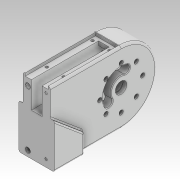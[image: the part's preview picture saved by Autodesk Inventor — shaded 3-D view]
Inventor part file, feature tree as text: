
AUTODESK INVENTOR PART (.ipt)
format: ipt  version: 2020 (Build 240168000, 168)  size: 836,608 bytes
history: native  units: mm
features: sketch x30, extrude x28, fillet x5, plane x2, revolve x2, pattern_circular x1, chamfer x1, projected_geometry x1
ambient origin geometry x8: Origin, YZ Plane, XZ Plane, XY Plane, X Axis, Y Axis, Z Axis, Center Point
bodies: Solid1 (feature_tree)
feature tree (70):
  extrude  "Extrusion1"  Depth=250.0mm
  extrude  "Extrusion3"  Depth=50.0mm TaperAngle=0.0deg
  extrude  "Extrusion6"  TaperAngle=0.0deg  [1 undecoded]
  extrude  "Extrusion7"  Depth=50.0mm
  extrude  "Extrusion8"  Depth=10.0mm TaperAngle=0.0deg
  extrude  "Extrusion9"  TaperAngle=0.0deg  [1 undecoded]
  extrude  "Extrusion10"  TaperAngle=30.0deg  [1 undecoded]
  extrude  "Extrusion11"  Depth=16.15mm
  extrude  "Extrusion12"  Depth=60.0mm
  plane  "Work Plane1"
  extrude  "Extrusion13"  Depth=10.0mm TaperAngle=0.0deg
  revolve  "Revolution1"  [1 undecoded]
  extrude  "Extrusion14"  Depth=86.0mm
  extrude  "Extrusion15"  Depth=4.0mm TaperAngle=0.0deg
  extrude  "Extrusion16"  Depth=70.0mm
  revolve  "Revolution2"  [1 undecoded]
  extrude  "Extrusion17"  Depth=7.3mm
  fillet  "Fillet1"  [1 undecoded]
  plane  "Work Plane2"
  extrude  "Extrusion18"  Depth=34.0mm
  extrude  "Extrusion19"  Depth=3.0mm TaperAngle=0.0deg
  extrude  "Extrusion20"  Depth=15.0mm TaperAngle=0.0deg
  extrude  "Extrusion21"  Depth=15.0mm
  extrude  "Extrusion25"  Depth=80.0mm TaperAngle=360.0deg
  extrude  "Extrusion22"  Depth=5.2mm
  fillet  "Fillet2"  Radius=5.2mm
  fillet  "Fillet3"  Radius=1.0mm
  extrude  "Extrusion23"  TaperAngle=90.0deg  [1 undecoded]
  extrude  "Extrusion24"  Depth=5.5mm
  extrude  "Extrusion26"  Depth=19.198622mm
  extrude  "Extrusion27"  Depth=50.0mm
  extrude  "Extrusion28"  TaperAngle=0.0deg  [1 undecoded]
  extrude  "CHOP"  Depth=14.0mm
  extrude  "Extrusion30"  Depth=12.5mm
  extrude  "Extrusion31"  Depth=1.0mm
  fillet  "Fillet4"  Radius=10.0mm
  pattern_circular  "Circular Pattern1"  [2 undecoded]
  chamfer  "Chamfer1"  Distance=32.0mm
  fillet  "Fillet5"  Radius=110.0mm
  sketch  "Sketch1"  dims[d0=50.0mm d1=250.0mm]
  sketch  "Sketch3"  dims[d2=47.2mm d3=50.0mm d4=0.0mm]
  sketch  "Sketch6"  dims[d10=5.0mm d11=0.0mm d12=0.0mm]
  sketch  "Sketch7"  dims[d19=50.0mm d20=0.0mm d21=8.726646mm]
  projected_geometry  "Projected Loop1"
  sketch  "Sketch8"  dims[d22=75.0mm d25=10.0mm d26=0.0mm]
  sketch  "Sketch9"  dims[d27=50.0mm d30=0.0mm d31=0.0mm]
  sketch  "Sketch10"  dims[d33=30.0deg d34=30.0deg]
  sketch  "Sketch11"  dims[d35=0.0mm d36=0.0mm d37=16.15mm]
  sketch  "Sketch12"  dims[d38=3.3mm d39=60.0mm]
  sketch  "Sketch13"  dims[d40=80.0mm d42=360.0deg d44=10.0mm d45=0.0mm]
  sketch  "Sketch14"  dims[d50=42.0mm d51=42.0mm d52=0.0mm d53=0.0mm]
  sketch  "Sketch15"  dims[d54=38.0mm d55=86.0mm]
  sketch  "Sketch16"  dims[d56=59.0mm d57=4.0mm d58=0.0mm]
  sketch  "Sketch17"  dims[d59=-2.0mm d60=70.0mm]
  sketch  "Sketch18"  dims[d61=40.0mm d62=18.0mm d63=0.0mm]
  sketch  "Sketch19"  dims[d64=1.5mm d65=7.3mm d66=90.0deg]
  sketch  "Sketch20"  dims[d67=22.0mm d68=34.0mm]
  sketch  "Sketch21"  dims[d69=3.5mm d70=3.0mm d71=0.0mm]
  sketch  "Sketch22"  dims[d72=0.0mm d73=15.0mm d74=0.0mm]
  sketch  "Sketch23"  dims[d75=15.0mm d76=130.0mm]
  sketch  "Sketch24"  dims[d77=6.0mm d78=80.0mm d80=360.0deg]
  sketch  "Sketch25"  dims[d82=15.0mm d83=0.0mm d84=5.2mm d85=5.2mm d86=1.0mm]
  sketch  "Sketch26"  dims[d87=1.5mm d88=90.0deg]
  sketch  "Sketch27"  dims[d89=5.5mm d90=20.0mm]
  sketch  "Sketch28"  dims[d91=30.0deg d92=19.198622mm]
  sketch  "Sketch29"  dims[d93=15.0mm d94=0.0mm d95=50.0mm]
  sketch  "Sketch30"  dims[d96=30.0mm d97=0.0mm]
  sketch  "Sketch31"  dims[d98=8.0mm d99=14.0mm]
  sketch  "Sketch32"  dims[d100=6.4mm d101=12.5mm]
  sketch  "Sketch33"  dims[d102=130.0mm d103=80.0mm d104=0.0mm d105=0.0mm d106=2.45mm d107=10.0mm d108=10.0mm d109=32.0mm d110=110.0mm d111=0.0mm d112=3.0mm d113=3.0mm d114=5.0mm d115=1.0mm d116=4.0mm d117=0.0mm d118=4.0mm d119=4.0mm d120=32.25mm d121=0.0mm d122=3.0mm d124=0.5mm d125=0.0mm d126=3.0mm d127=2.0mm d128=8.0mm d129=8.0mm d130=4.0mm d131=4.0mm d132=3.9mm d133=6.0mm d134=0.0mm d135=4.0mm d136=0.0mm d137=60.0mm d138=0.5mm d139=0.0mm d140=3.0mm d141=10.0mm d142=20.0mm d143=15.0mm d144=0.0mm d145=8.0mm d146=23.75mm d147=0.0mm d148=15.0mm d149=23.75mm d150=0.0mm d151=200.998mm d152=0.0mm d153=76.0mm d154=4.0mm d155=1.0mm d156=0.0mm d157=22.5mm d158=2.0mm d159=15.0mm d160=0.8mm d161=0.0mm d162=0.2mm d163=80.0mm d164=360.0deg d166=0.5mm d167=2.0mm d168=45.0deg d169=1.0mm d123=0.872665mm]
note: 10 required parameter values undecoded (feature->parameter linkage not recoverable at this tier; creation-order binding heuristic only, values carry confidence <= 0.55)